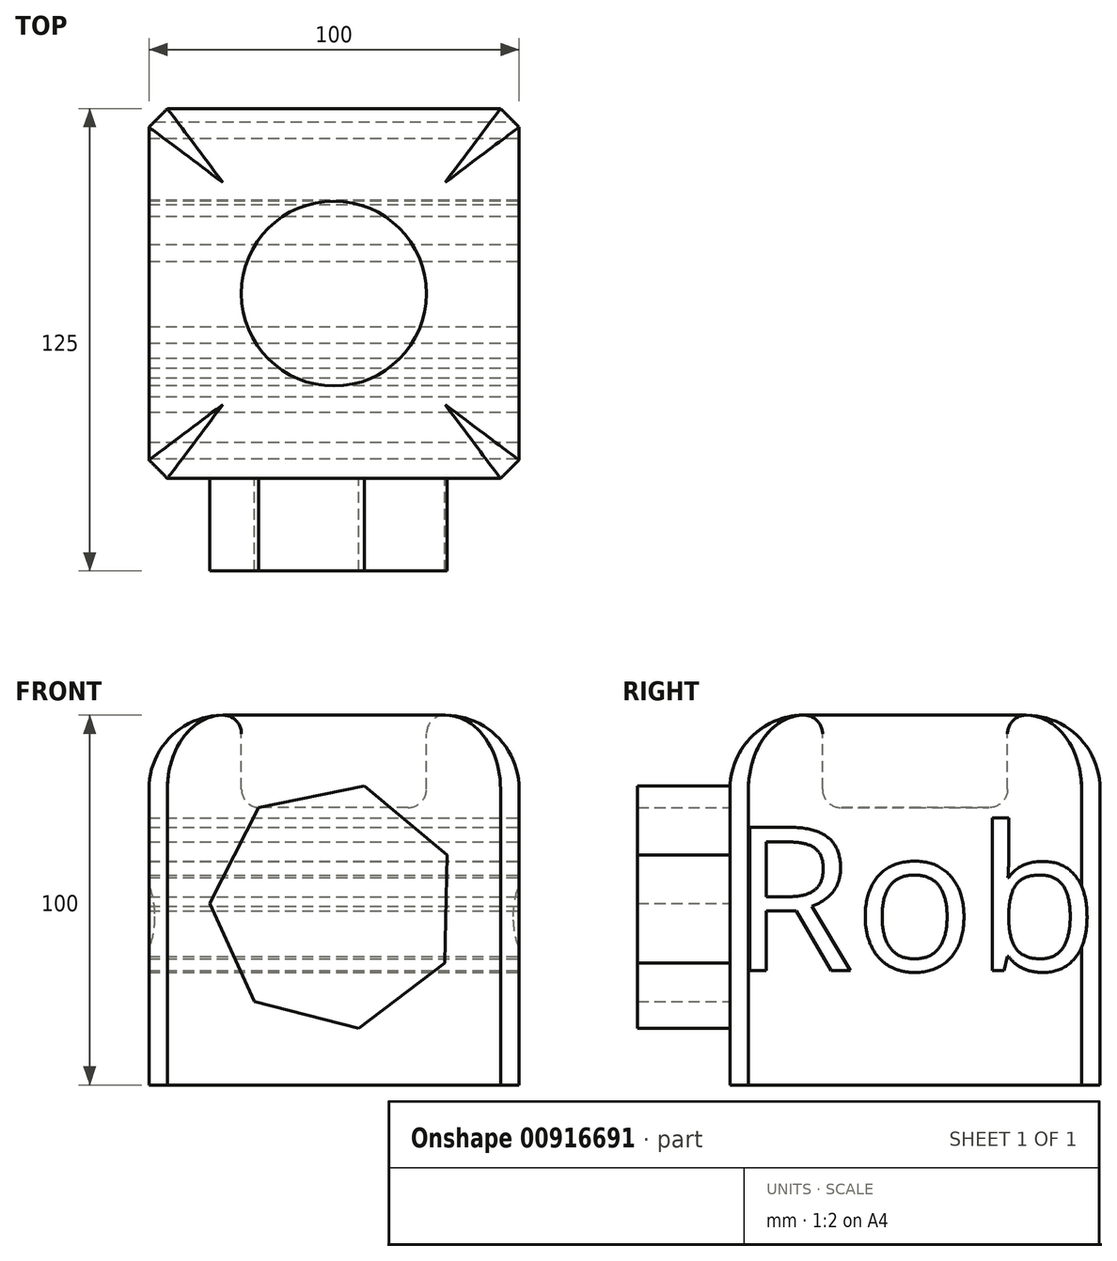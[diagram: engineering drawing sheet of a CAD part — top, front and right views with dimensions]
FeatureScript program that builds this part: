
annotation { "Feature Type Name" : "Feature", "Feature Type Description" : "" }
export const myFeature = defineFeature(function(context is Context, id is Id, definition is map)
    precondition{}
    {
        {
            var Q0;
            Q0=qCreatedBy(makeId("Top.planeOp"),FACE);
            var sketch = newSketch(context, id + "F0", { "sketchPlane" : qUnion([Q0])});
            skLineSegment(sketch, "E0.bottom", {"start": v(50, -50) * mm, "end": v(-50, -50) * mm});
            skLineSegment(sketch, "E0.top", {"start": v(50, 50) * mm, "end": v(-50, 50) * mm});
            skLineSegment(sketch, "E0.left", {"start": v(50, -50) * mm, "end": v(50, 50) * mm});
            skLineSegment(sketch, "E0.right", {"start": v(-50, -50) * mm, "end": v(-50, 50) * mm});
            skPoint(sketch, "E0.middle", {"position": v(0, 0) * mm});
            skSolve(sketch);
        }
        {
            var Q0;
            Q0=makeQuery(id+"F0.imprint","IMPRINT",FACE,{"disambiguationData":[TD([[makeQuery(id+"F0.imprint","IMPRINT",EDGE,{"derivedFrom":sQuery(id+"F0.wireOp",EDGE,"E0.bottom")}),-1.0]])]});
            extrude(context, id + "F1", {"entities" : qUnion([Q0]), "depth" : 100 * mm, "offsetDistance" : 25 * mm});
        }
        {
            var Q0;
            Q0=makeQuery(id+"F1.opExtrude","CAP_FACE",FACE,{"disambiguationData":[OSD([sQuery(id+"F0.wireOp",EDGE,"E0.bottom"),sQuery(id+"F0.wireOp",EDGE,"E0.top"),sQuery(id+"F0.wireOp",EDGE,"E0.left"),sQuery(id+"F0.wireOp",EDGE,"E0.right")])],"isStart":false});
            var sketch = newSketch(context, id + "F2", { "sketchPlane" : qUnion([Q0])});
            skCircle(sketch, "E1", {"center": v(0, 0) * mm, "radius": 25 * mm});
            skSolve(sketch);
        }
        {
            var Q0;
            Q0=makeQuery(id+"F2.imprint","IMPRINT",FACE,{"disambiguationData":[TD([[makeQuery(id+"F2.imprint","IMPRINT",EDGE,{"derivedFrom":sQuery(id+"F2.wireOp",EDGE,"E1")}),1.0]])]});
            extrude(context, id + "F3", {"entities" : qUnion([Q0]), "operationType" : NewBodyOperationType.REMOVE, "oppositeDirection" : true, "depth" : 25 * mm, "offsetDistance" : 25 * mm});
        }
        {
            var Q0;
            Q0=makeQuery(id+"F1.opExtrude","SWEPT_FACE",FACE,{"disambiguationData":[OSD([sQuery(id+"F0.wireOp",EDGE,"E0.bottom")])]});
            var sketch = newSketch(context, id + "F4", { "sketchPlane" : qUnion([Q0])});
            skCircle(sketch, "E2.cCircle", {"center": v(0, 48.28) * mm, "radius": 30.26 * mm, "construction": true});
            skLineSegment(sketch, "E2.0", {"start": v(-33.57, 49.09) * mm, "end": v(-20.3, 75.03) * mm});
            skLineSegment(sketch, "E2.1", {"start": v(-20.3, 75.03) * mm, "end": v(8.25, 80.83) * mm});
            skLineSegment(sketch, "E2.2", {"start": v(8.25, 80.83) * mm, "end": v(30.6, 62.13) * mm});
            skLineSegment(sketch, "E2.3", {"start": v(30.6, 62.13) * mm, "end": v(29.9, 33) * mm});
            skLineSegment(sketch, "E2.4", {"start": v(29.9, 33) * mm, "end": v(6.69, 15.38) * mm});
            skLineSegment(sketch, "E2.5", {"start": v(6.69, 15.38) * mm, "end": v(-21.56, 22.54) * mm});
            skLineSegment(sketch, "E2.6", {"start": v(-21.56, 22.54) * mm, "end": v(-33.57, 49.09) * mm});
            skPoint(sketch, "E2.0.midPoint", {"position": v(-26.94, 62.06) * mm});
            skSolve(sketch);
        }
        {
            var Q0;
            Q0 = qSketchRegion(id + "F4", true);
            extrude(context, id + "F5", {"entities" : qUnion([Q0]), "operationType" : NewBodyOperationType.ADD, "depth" : 25 * mm, "offsetDistance" : 25 * mm});
        }
        {
            var Q0;
            Q0=makeQuery(id+"F1.opExtrude","SWEPT_FACE",FACE,{"disambiguationData":[OSD([sQuery(id+"F0.wireOp",EDGE,"E0.left")])]});
            var sketch = newSketch(context, id + "F6", { "sketchPlane" : qUnion([Q0])});
            skText(sketch, "E3", { "text": "Rob", "fontName": "OpenSans-Regular.ttf"});
            const initialGuessF6  = {"E3": [-0.05, 0.03096, 1, 0, 0.03904]};
            skSetInitialGuess(sketch, initialGuessF6);
            skSolve(sketch);
        }
        {
            var Q0;
            Q0 = qSketchRegion(id + "F6", true);
            extrude(context, id + "F7", {"entities" : qUnion([Q0]), "operationType" : NewBodyOperationType.REMOVE, "oppositeDirection" : true, "depth" : 25 * mm, "offsetDistance" : 25 * mm});
        }
        {
            var Q0;
            Q0=makeQuery(id+"F1.opExtrude","CAP_EDGE",EDGE,{"disambiguationData":[OSD([sQuery(id+"F0.wireOp",EDGE,"E0.bottom")])],"isStart":false});
            var Q1;
            Q1=makeQuery(id+"F1.opExtrude","CAP_EDGE",EDGE,{"disambiguationData":[OSD([sQuery(id+"F0.wireOp",EDGE,"E0.left")])],"isStart":false});
            var Q2;
            Q2=makeQuery(id+"F1.opExtrude","CAP_EDGE",EDGE,{"disambiguationData":[OSD([sQuery(id+"F0.wireOp",EDGE,"E0.top")])],"isStart":false});
            var Q3;
            Q3=makeQuery(id+"F1.opExtrude","CAP_EDGE",EDGE,{"disambiguationData":[OSD([sQuery(id+"F0.wireOp",EDGE,"E0.right")])],"isStart":false});
            fillet(context, id + "F8", {"entities" : qUnion([Q0, Q1, Q2, Q3]), "radius" : 20 * mm, "tangentPropagation" : true, "allowEdgeOverflow" : false});
        }
        {
            var Q0;
            Q0=makeQuery(id+"F3.boolean.opBoolean","COPY",EDGE,{"derivedFrom":makeQuery(id+"F3.opExtrude","CAP_EDGE",EDGE,{"disambiguationData":[OSD([sQuery(id+"F2.wireOp",EDGE,"E1")])],"isStart":true})});
            var Q1;
            Q1=makeQuery(id+"F3.boolean.opBoolean","COPY",FACE,{"derivedFrom":makeQuery(id+"F3.opExtrude","SWEPT_FACE",FACE,{"disambiguationData":[OSD([sQuery(id+"F2.wireOp",EDGE,"E1")])]})});
            fillet(context, id + "F9", {"entities" : qUnion([Q0, Q1]), "radius" : 5 * mm, "tangentPropagation" : true, "allowEdgeOverflow" : false});
        }
        {
            var Q0;
            Q0=makeQuery(id+"F7.boolean.opBoolean","COPY",FACE,{"derivedFrom":makeQuery(id+"F7.opExtrude","CAP_FACE",FACE,{"disambiguationData":[OSD([sQuery(id+"F6.wireOp",EDGE,"E3.sketch_text.stroke-0"),sQuery(id+"F6.wireOp",EDGE,"E3.sketch_text.stroke-1"),sQuery(id+"F6.wireOp",EDGE,"E3.sketch_text.stroke-2"),sQuery(id+"F6.wireOp",EDGE,"E3.sketch_text.stroke-3"),sQuery(id+"F6.wireOp",EDGE,"E3.sketch_text.stroke-4"),sQuery(id+"F6.wireOp",EDGE,"E3.sketch_text.stroke-5"),sQuery(id+"F6.wireOp",EDGE,"E3.sketch_text.stroke-6"),sQuery(id+"F6.wireOp",EDGE,"E3.sketch_text.stroke-7"),sQuery(id+"F6.wireOp",EDGE,"E3.sketch_text.stroke-8"),sQuery(id+"F6.wireOp",EDGE,"E3.sketch_text.stroke-9"),sQuery(id+"F6.wireOp",EDGE,"E3.sketch_text.stroke-10"),sQuery(id+"F6.wireOp",EDGE,"E3.sketch_text.stroke-11"),sQuery(id+"F6.wireOp",EDGE,"E3.sketch_text.stroke-12"),sQuery(id+"F6.wireOp",EDGE,"E3.sketch_text.stroke-13"),sQuery(id+"F6.wireOp",EDGE,"E3.sketch_text.stroke-14"),sQuery(id+"F6.wireOp",EDGE,"E3.sketch_text.stroke-15"),sQuery(id+"F6.wireOp",EDGE,"E3.sketch_text.stroke-16"),sQuery(id+"F6.wireOp",EDGE,"E3.sketch_text.stroke-17")])],"isStart":false})});
            extrude(context, id + "F10", {"entities" : qUnion([Q0]), "operationType" : NewBodyOperationType.REMOVE, "oppositeDirection" : true, "depth" : 100 * mm, "offsetDistance" : 25 * mm});
        }
        {
            var Q0;
            Q0=makeQuery(id+"F7.boolean.opBoolean","COPY",FACE,{"derivedFrom":makeQuery(id+"F7.opExtrude","CAP_FACE",FACE,{"disambiguationData":[OSD([sQuery(id+"F6.wireOp",EDGE,"E3.sketch_text.stroke-18"),sQuery(id+"F6.wireOp",EDGE,"E3.sketch_text.stroke-19"),sQuery(id+"F6.wireOp",EDGE,"E3.sketch_text.stroke-20"),sQuery(id+"F6.wireOp",EDGE,"E3.sketch_text.stroke-21"),sQuery(id+"F6.wireOp",EDGE,"E3.sketch_text.stroke-22"),sQuery(id+"F6.wireOp",EDGE,"E3.sketch_text.stroke-23"),sQuery(id+"F6.wireOp",EDGE,"E3.sketch_text.stroke-24"),sQuery(id+"F6.wireOp",EDGE,"E3.sketch_text.stroke-25"),sQuery(id+"F6.wireOp",EDGE,"E3.sketch_text.stroke-26"),sQuery(id+"F6.wireOp",EDGE,"E3.sketch_text.stroke-27"),sQuery(id+"F6.wireOp",EDGE,"E3.sketch_text.stroke-28"),sQuery(id+"F6.wireOp",EDGE,"E3.sketch_text.stroke-29"),sQuery(id+"F6.wireOp",EDGE,"E3.sketch_text.stroke-30"),sQuery(id+"F6.wireOp",EDGE,"E3.sketch_text.stroke-31"),sQuery(id+"F6.wireOp",EDGE,"E3.sketch_text.stroke-32"),sQuery(id+"F6.wireOp",EDGE,"E3.sketch_text.stroke-33"),sQuery(id+"F6.wireOp",EDGE,"E3.sketch_text.stroke-34")])],"isStart":false})});
            extrude(context, id + "F11", {"entities" : qUnion([Q0]), "operationType" : NewBodyOperationType.REMOVE, "oppositeDirection" : true, "depth" : 100 * mm, "offsetDistance" : 25 * mm});
        }
        {
            var Q0;
            Q0=makeQuery(id+"F7.boolean.opBoolean","COPY",FACE,{"derivedFrom":makeQuery(id+"F7.opExtrude","CAP_FACE",FACE,{"disambiguationData":[OSD([sQuery(id+"F6.wireOp",EDGE,"E3.sketch_text.stroke-35"),sQuery(id+"F6.wireOp",EDGE,"E3.sketch_text.stroke-36"),sQuery(id+"F6.wireOp",EDGE,"E3.sketch_text.stroke-37"),sQuery(id+"F6.wireOp",EDGE,"E3.sketch_text.stroke-38"),sQuery(id+"F6.wireOp",EDGE,"E3.sketch_text.stroke-39"),sQuery(id+"F6.wireOp",EDGE,"E3.sketch_text.stroke-40"),sQuery(id+"F6.wireOp",EDGE,"E3.sketch_text.stroke-41"),sQuery(id+"F6.wireOp",EDGE,"E3.sketch_text.stroke-42"),sQuery(id+"F6.wireOp",EDGE,"E3.sketch_text.stroke-43"),sQuery(id+"F6.wireOp",EDGE,"E3.sketch_text.stroke-44"),sQuery(id+"F6.wireOp",EDGE,"E3.sketch_text.stroke-45"),sQuery(id+"F6.wireOp",EDGE,"E3.sketch_text.stroke-46"),sQuery(id+"F6.wireOp",EDGE,"E3.sketch_text.stroke-47"),sQuery(id+"F6.wireOp",EDGE,"E3.sketch_text.stroke-48"),sQuery(id+"F6.wireOp",EDGE,"E3.sketch_text.stroke-49"),sQuery(id+"F6.wireOp",EDGE,"E3.sketch_text.stroke-50"),sQuery(id+"F6.wireOp",EDGE,"E3.sketch_text.stroke-51"),sQuery(id+"F6.wireOp",EDGE,"E3.sketch_text.stroke-52"),sQuery(id+"F6.wireOp",EDGE,"E3.sketch_text.stroke-53"),sQuery(id+"F6.wireOp",EDGE,"E3.sketch_text.stroke-54"),sQuery(id+"F6.wireOp",EDGE,"E3.sketch_text.stroke-55"),sQuery(id+"F6.wireOp",EDGE,"E3.sketch_text.stroke-56"),sQuery(id+"F6.wireOp",EDGE,"E3.sketch_text.stroke-57")])],"isStart":false})});
            extrude(context, id + "F12", {"entities" : qUnion([Q0]), "operationType" : NewBodyOperationType.REMOVE, "oppositeDirection" : true, "depth" : 25 * mm, "offsetDistance" : 25 * mm});
        }
        {
            var Q0;
            Q0=makeQuery(id+"F12.boolean.opBoolean","COPY",FACE,{"derivedFrom":makeQuery(id+"F12.opExtrude","CAP_FACE",FACE,{"disambiguationData":[OSD([sQuery(id+"F6.wireOp",EDGE,"E3.sketch_text.stroke-35"),sQuery(id+"F6.wireOp",EDGE,"E3.sketch_text.stroke-36"),sQuery(id+"F6.wireOp",EDGE,"E3.sketch_text.stroke-37"),sQuery(id+"F6.wireOp",EDGE,"E3.sketch_text.stroke-38"),sQuery(id+"F6.wireOp",EDGE,"E3.sketch_text.stroke-39"),sQuery(id+"F6.wireOp",EDGE,"E3.sketch_text.stroke-40"),sQuery(id+"F6.wireOp",EDGE,"E3.sketch_text.stroke-41"),sQuery(id+"F6.wireOp",EDGE,"E3.sketch_text.stroke-42"),sQuery(id+"F6.wireOp",EDGE,"E3.sketch_text.stroke-43"),sQuery(id+"F6.wireOp",EDGE,"E3.sketch_text.stroke-44"),sQuery(id+"F6.wireOp",EDGE,"E3.sketch_text.stroke-45"),sQuery(id+"F6.wireOp",EDGE,"E3.sketch_text.stroke-46"),sQuery(id+"F6.wireOp",EDGE,"E3.sketch_text.stroke-47"),sQuery(id+"F6.wireOp",EDGE,"E3.sketch_text.stroke-48"),sQuery(id+"F6.wireOp",EDGE,"E3.sketch_text.stroke-49"),sQuery(id+"F6.wireOp",EDGE,"E3.sketch_text.stroke-50"),sQuery(id+"F6.wireOp",EDGE,"E3.sketch_text.stroke-51"),sQuery(id+"F6.wireOp",EDGE,"E3.sketch_text.stroke-52"),sQuery(id+"F6.wireOp",EDGE,"E3.sketch_text.stroke-53"),sQuery(id+"F6.wireOp",EDGE,"E3.sketch_text.stroke-54"),sQuery(id+"F6.wireOp",EDGE,"E3.sketch_text.stroke-55"),sQuery(id+"F6.wireOp",EDGE,"E3.sketch_text.stroke-56"),sQuery(id+"F6.wireOp",EDGE,"E3.sketch_text.stroke-57")])],"isStart":false})});
            extrude(context, id + "F13", {"entities" : qUnion([Q0]), "operationType" : NewBodyOperationType.REMOVE, "oppositeDirection" : true, "depth" : 100 * mm, "offsetDistance" : 25 * mm});
        }
        {
            var Q0;
            Q0=makeQuery(id+"F1.opExtrude","SWEPT_EDGE",EDGE,{"disambiguationData":[OSD([sQuery(id+"F0.wireOp",EDGE,"E0.bottom"),sQuery(id+"F0.wireOp",EDGE,"E0.left")])]});
            var Q1;
            Q1=makeQuery(id+"F1.opExtrude","SWEPT_EDGE",EDGE,{"disambiguationData":[OSD([sQuery(id+"F0.wireOp",EDGE,"E0.top"),sQuery(id+"F0.wireOp",EDGE,"E0.left")])]});
            var Q2;
            Q2=makeQuery(id+"F1.opExtrude","SWEPT_EDGE",EDGE,{"disambiguationData":[OSD([sQuery(id+"F0.wireOp",EDGE,"E0.top"),sQuery(id+"F0.wireOp",EDGE,"E0.right")])]});
            var Q3;
            Q3=makeQuery(id+"F1.opExtrude","SWEPT_EDGE",EDGE,{"disambiguationData":[OSD([sQuery(id+"F0.wireOp",EDGE,"E0.bottom"),sQuery(id+"F0.wireOp",EDGE,"E0.right")])]});
            chamfer(context, id + "F14", {"entities" : qUnion([Q0, Q1, Q2, Q3]), "width" : 5 * mm, "tangentPropagation" : true});
        }
    });
